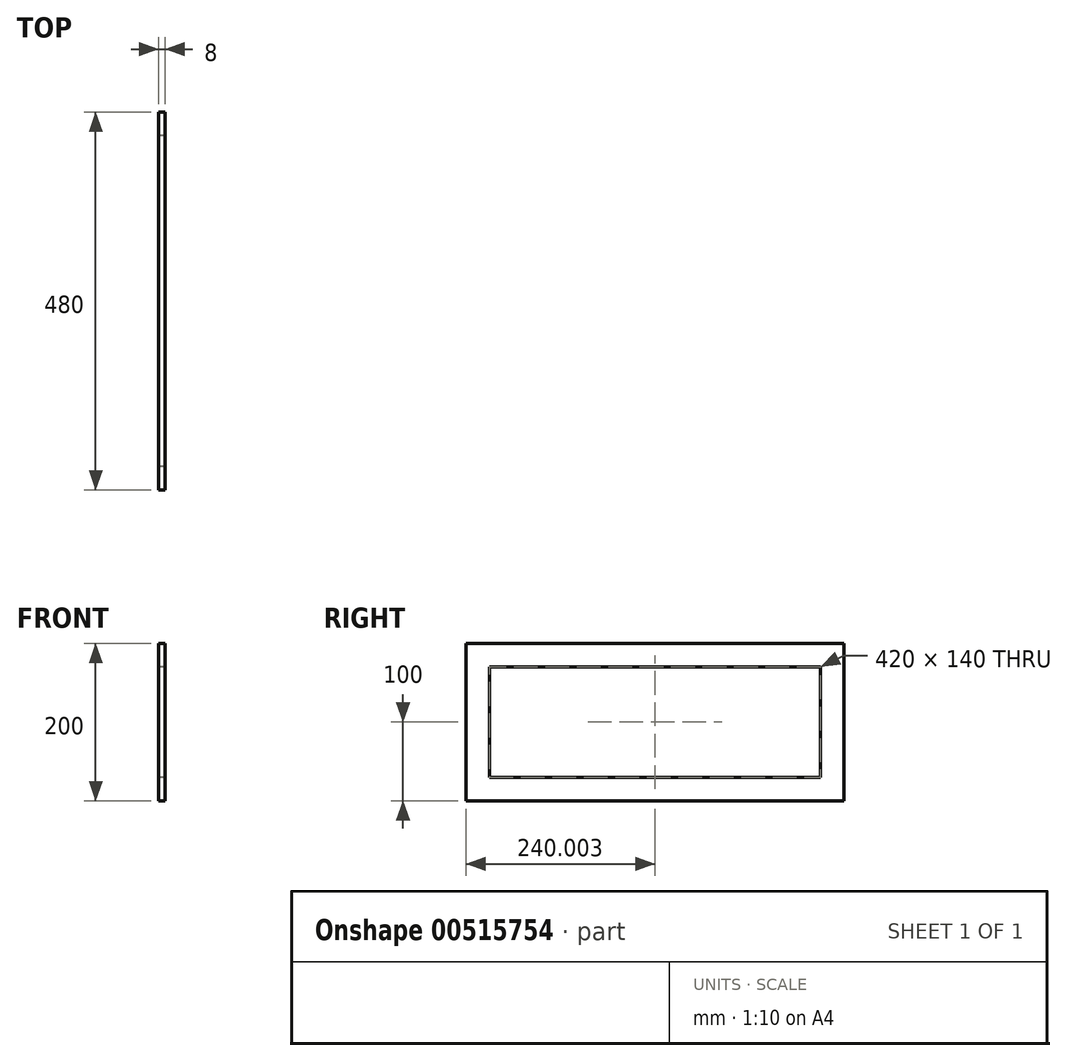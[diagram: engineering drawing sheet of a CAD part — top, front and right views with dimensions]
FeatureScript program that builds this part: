
annotation { "Feature Type Name" : "Feature", "Feature Type Description" : "" }
export const myFeature = defineFeature(function(context is Context, id is Id, definition is map)
    precondition{}
    {
        {
            var Q0;
            Q0=qCreatedBy(makeId("Right.planeOp"),FACE);
            var sketch = newSketch(context, id + "F0", { "sketchPlane" : qUnion([Q0])});
            skLineSegment(sketch, "E0.bottom", {"start": v(-277.39, 200) * mm, "end": v(202.61, 200) * mm});
            skLineSegment(sketch, "E0.top", {"start": v(-277.39, 0) * mm, "end": v(202.61, 0) * mm});
            skLineSegment(sketch, "E0.left", {"start": v(-277.39, 200) * mm, "end": v(-277.39, 0) * mm});
            skLineSegment(sketch, "E0.right", {"start": v(202.61, 200) * mm, "end": v(202.61, 0) * mm});
            skLineSegment(sketch, "E1.0", {"start": v(-247.39, 170) * mm, "end": v(172.61, 170) * mm});
            skLineSegment(sketch, "E1.1", {"start": v(-247.39, 170) * mm, "end": v(-247.39, 30) * mm});
            skLineSegment(sketch, "E1.2", {"start": v(-247.39, 30) * mm, "end": v(172.61, 30) * mm});
            skLineSegment(sketch, "E1.3", {"start": v(172.61, 170) * mm, "end": v(172.61, 30) * mm});
            skLineSegment(sketch, "E2", {"start": v(-37.39, 200) * mm, "end": v(-37.39, 0) * mm, "construction": true});
            skLineSegment(sketch, "E3", {"start": v(-107.39, 170) * mm, "end": v(-107.39, 30) * mm});
            skLineSegment(sketch, "E4", {"start": v(32.61, 170) * mm, "end": v(32.61, 30) * mm});
            skSolve(sketch);
        }
        {
            var Q0;
            Q0=makeQuery(id+"F0.imprint","IMPRINT",FACE,{"disambiguationData":[TD([[makeQuery(id+"F0.imprint","IMPRINT",EDGE,{"derivedFrom":sQuery(id+"F0.wireOp",EDGE,"E0.bottom")}),-1.0]])]});
            extrude(context, id + "F1", {"entities" : qUnion([Q0]), "depth" : 8 * mm, "offsetDistance" : 25 * mm});
        }
    });
